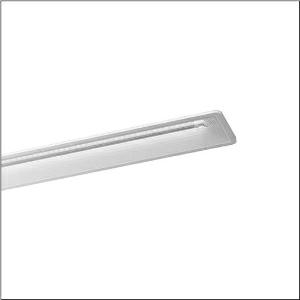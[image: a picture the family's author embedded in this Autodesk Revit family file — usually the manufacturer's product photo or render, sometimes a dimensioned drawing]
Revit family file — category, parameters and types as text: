
# Revit family: taris_r__21_5mt115d03wd_575d
name_source: partatom
category: Lighting Fixtures
units: mm (PartAtom-declared; Revit-internal decimal feet)

## family parameters
Cut with Voids When Loaded = No
Host = Face
Light Source = No
Part Type = Normal
Room Calculation Point = No
Round Connector Dimension = Use Diameter
Shared = No

## types (1)
- --- (1 x LED, 3420 lm, 22.2 W, 3000K)
    Apparent Load = 22 VA
    CIE Flux Codes = 73 96 99 100 100
    Color Rendering = 80
    Color Temperature = 3000K
    Default Elevation = 1800 mm
    Description = Taris® 21, office luminaire, primary anti-glare with micro louvre, primary optical cover: axial lens, of PMMA, structured, CAT 2 (L<= 1500cd/m²), light emission: direct distribution, primary light characteristic: symmetric, installation type: recessed, LED, rated luminous flux: 3.420lm, luminous efficacy: 154lm/W, light colour: 830, colour temperature: 3000K, control gear: ECG DALI, with terminal, 5-pole, mains connection: 230V, AC, 50Hz, rated input power: 22W, housing, luminaire housing, of plastic, traffic white (RAL 9016), length: 968mm, width: 150mm, height: 76mm, recess depth: 106mm, protection rating (complete): IP20, insulation class (complete): insulation class I (protective earthing), certification: CE, ENEC, VDE, protection symbol: F, impact resistance: IK02, permissible operating ambient temperature: 0..+35°C, standard: EN 50419, packaging unit: 1 piece
    Height = 0 mm  [stored 0 ft]
    Lamp = 1 x LED
    Lamp Light Flux = 3420 lm
    Lamp Power = 22.2 W
    Lamp count = 1
    Length = 962 mm
    Luminous efficacy = 154 lm/W
    Manufacturer = Siteco
    ModVariant = No
    Model = 5MT115D03WD
    Mounting Place = Ceiling
    Mounting Type = Recessed
    Number of Poles = 1
    OnlyDefault = Yes
    Power Factor = 1
    Product Name = Taris® 21
    Product group = office luminaire | ceiling recessed
    ProductGroupID = 401
    Protection Class = Protection class I
    Protection Degree = IP 20
    RLX_Detail_Level = 1
    RLX_Emergency_Light_Flux = 0 lm
    RLX_Emergency_Type = 0
    RLX_Emergency_Type_DB = No
    RlxData = <blob elided: 29673 chars, md5=ca2253ec>
    Socket = socket
    Standby Power = 0 W
    System Light Flux = 3420 lm
    System Power = 22 W
    Type Comments = factory setting: luminous flux: 100 % | dim-lin: 254 | 200 mA
    Type Image = l_1004723.jpg
    URL = http://relux.com
    VarID = @adj_137103
    Voltage = 0 V
    Weight = 0.00 kg
    Width = 144 mm

note: [stored X ft] marks values corroborated as IEEE doubles in the binary element streams (Revit-internal decimal feet)

## geometry (parser evidence)
native form markers: Blend x4, Sweep x10
no freeform markers — native parametric forms only
